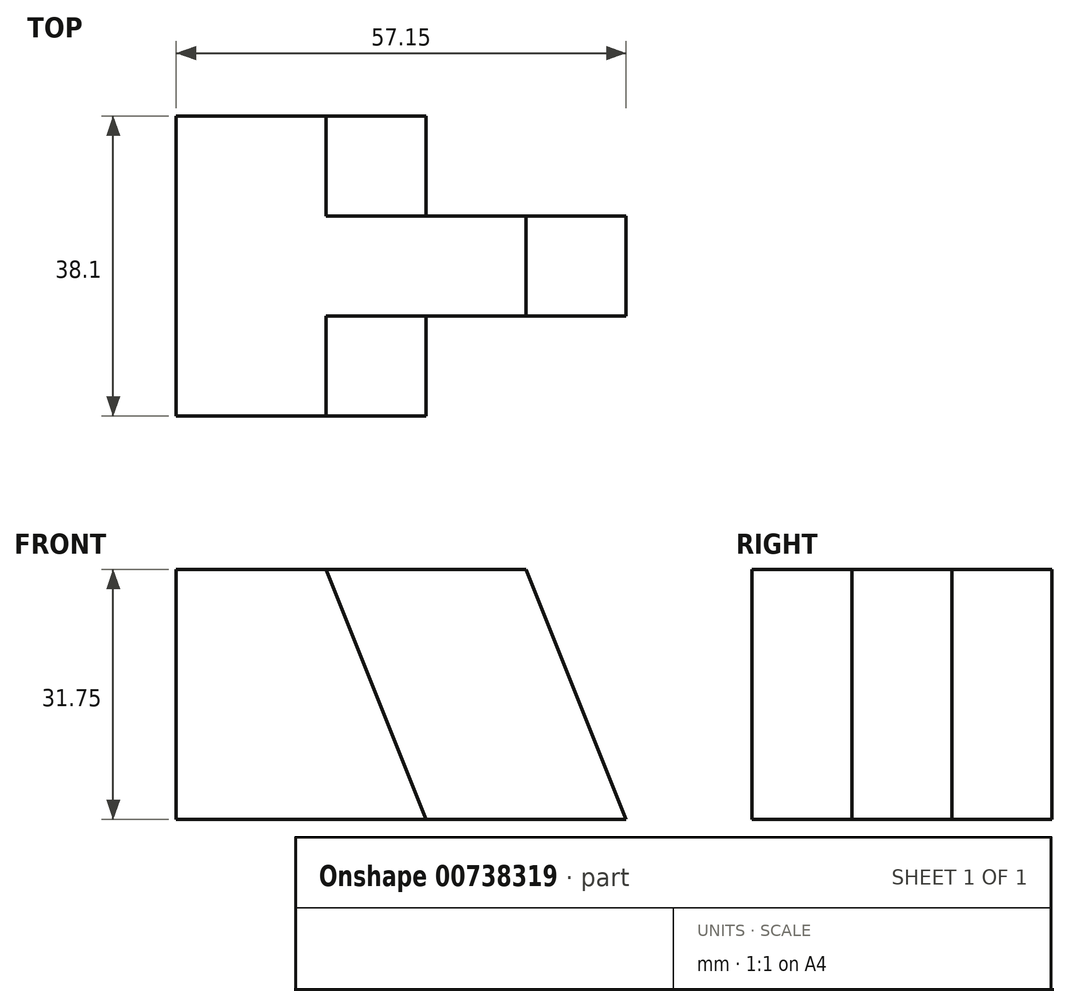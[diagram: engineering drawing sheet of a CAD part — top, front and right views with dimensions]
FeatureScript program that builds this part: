
annotation { "Feature Type Name" : "Feature", "Feature Type Description" : "" }
export const myFeature = defineFeature(function(context is Context, id is Id, definition is map)
    precondition{}
    {
        {
            var Q0;
            Q0=qCreatedBy(makeId("Top.planeOp"),FACE);
            var sketch = newSketch(context, id + "F0", { "sketchPlane" : qUnion([Q0])});
            skLineSegment(sketch, "E0", {"start": v(-31.75, 0) * mm, "end": v(-31.75, -38.1) * mm});
            skLineSegment(sketch, "E1", {"start": v(-31.75, -38.1) * mm, "end": v(0, -38.1) * mm});
            skLineSegment(sketch, "E2", {"start": v(0, -38.1) * mm, "end": v(0, -25.4) * mm});
            skLineSegment(sketch, "E3", {"start": v(0, -25.4) * mm, "end": v(25.4, -25.4) * mm});
            skLineSegment(sketch, "E4", {"start": v(25.4, -25.4) * mm, "end": v(25.4, -12.7) * mm});
            skLineSegment(sketch, "E5", {"start": v(25.4, -12.7) * mm, "end": v(0, -12.7) * mm});
            skLineSegment(sketch, "E6", {"start": v(0, -12.7) * mm, "end": v(0, 0) * mm});
            skLineSegment(sketch, "E7", {"start": v(0, 0) * mm, "end": v(-31.75, 0) * mm});
            skSolve(sketch);
        }
        {
            var Q0;
            Q0=makeQuery(id+"F0.imprint","IMPRINT",FACE,{"disambiguationData":[TD([[makeQuery(id+"F0.imprint","IMPRINT",EDGE,{"derivedFrom":sQuery(id+"F0.wireOp",EDGE,"E0")}),1.0]])]});
            extrude(context, id + "F1", {"entities" : qUnion([Q0]), "depth" : 31.75 * mm, "offsetDistance" : 25.4 * mm});
        }
        {
            var Q0;
            Q0=makeQuery(id+"F1.opExtrude","SWEPT_FACE",FACE,{"disambiguationData":[OSD([sQuery(id+"F0.wireOp",EDGE,"E1")])]});
            var sketch = newSketch(context, id + "F2", { "sketchPlane" : qUnion([Q0])});
            skLineSegment(sketch, "E8", {"start": v(-12.7, 31.75) * mm, "end": v(0, 0) * mm});
            skLineSegment(sketch, "E9", {"start": v(-12.7, 31.75) * mm, "end": v(0, 31.75) * mm});
            skSolve(sketch);
        }
        {
            var Q0;
            Q0=makeQuery(id+"F2.imprint","IMPRINT",FACE,{"disambiguationData":[TD([[makeQuery(id+"F2.imprint","IMPRINT",EDGE,{"derivedFrom":sQuery(id+"F2.wireOp",EDGE,"E8")}),1.0]])]});
            extrude(context, id + "F3", {"entities" : qUnion([Q0]), "operationType" : NewBodyOperationType.REMOVE, "oppositeDirection" : true, "depth" : 12.7 * mm, "offsetDistance" : 25.4 * mm});
        }
        {
            var Q0;
            Q0=makeQuery(id+"F3.boolean.opBoolean","MERGE",FACE,{"derivedFrom":[makeQuery(id+"F1.opExtrude","SWEPT_FACE",FACE,{"disambiguationData":[OSD([sQuery(id+"F0.wireOp",EDGE,"E3")])]}),makeQuery(id+"F3.opExtrude","CAP_FACE",FACE,{"disambiguationData":[OSD([sQuery(id+"F0.wireOp",EDGE,"E1"),sQuery(id+"F0.wireOp",EDGE,"E2"),sQuery(id+"F2.wireOp",EDGE,"E8"),sQuery(id+"F2.wireOp",EDGE,"E9")])],"isStart":false})]});
            var sketch = newSketch(context, id + "F4", { "sketchPlane" : qUnion([Q0])});
            skLineSegment(sketch, "E10", {"start": v(12.7, 31.75) * mm, "end": v(25.4, 0) * mm});
            skLineSegment(sketch, "E11", {"start": v(12.7, 31.75) * mm, "end": v(25.4, 31.75) * mm});
            skSolve(sketch);
        }
        {
            var Q0;
            Q0=makeQuery(id+"F4.imprint","IMPRINT",FACE,{"disambiguationData":[TD([[makeQuery(id+"F4.imprint","IMPRINT",EDGE,{"derivedFrom":sQuery(id+"F4.wireOp",EDGE,"E10")}),1.0]])]});
            extrude(context, id + "F5", {"entities" : qUnion([Q0]), "operationType" : NewBodyOperationType.REMOVE, "endBound" : BoundingType.THROUGH_ALL, "oppositeDirection" : true, "depth" : 25.4 * mm, "offsetDistance" : 25.4 * mm});
        }
        {
            var Q0;
            Q0=makeQuery(id+"F1.opExtrude","SWEPT_FACE",FACE,{"disambiguationData":[OSD([sQuery(id+"F0.wireOp",EDGE,"E7")])]});
            var sketch = newSketch(context, id + "F6", { "sketchPlane" : qUnion([Q0])});
            skLineSegment(sketch, "E12", {"start": v(0, 0) * mm, "end": v(12.7, 31.75) * mm});
            skLineSegment(sketch, "E13", {"start": v(12.7, 31.75) * mm, "end": v(0, 31.75) * mm});
            skSolve(sketch);
        }
        {
            var Q0;
            Q0=makeQuery(id+"F6.imprint","IMPRINT",FACE,{"disambiguationData":[TD([[makeQuery(id+"F6.imprint","IMPRINT",EDGE,{"derivedFrom":sQuery(id+"F6.wireOp",EDGE,"E12")}),1.0]])]});
            extrude(context, id + "F7", {"entities" : qUnion([Q0]), "operationType" : NewBodyOperationType.REMOVE, "oppositeDirection" : true, "depth" : 12.7 * mm, "offsetDistance" : 25.4 * mm});
        }
    });
